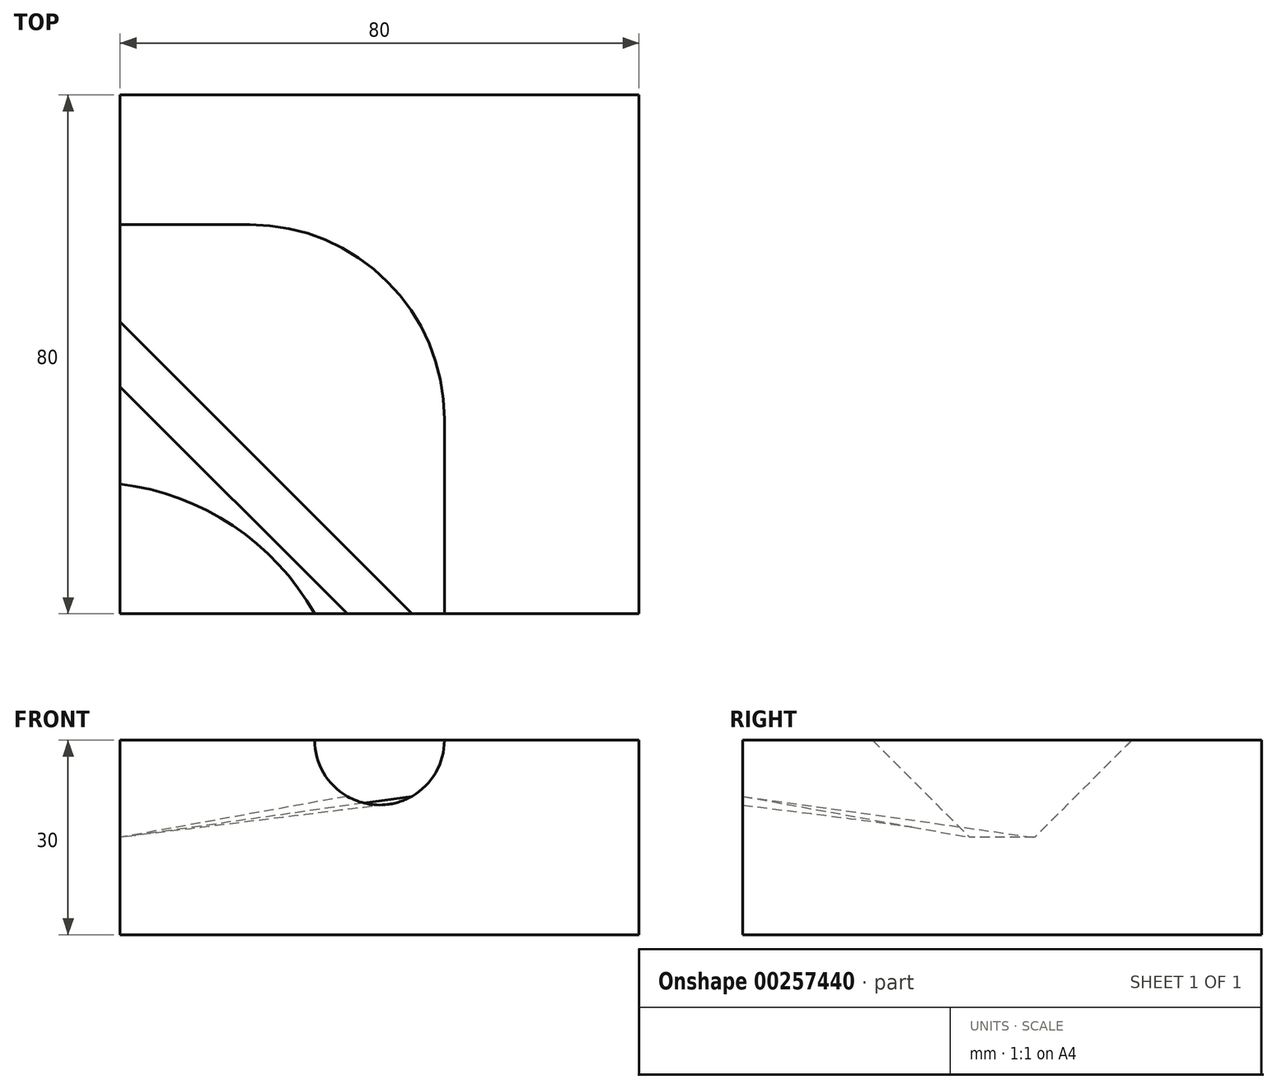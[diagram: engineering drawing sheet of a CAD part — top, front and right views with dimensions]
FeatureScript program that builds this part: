
annotation { "Feature Type Name" : "Feature", "Feature Type Description" : "" }
export const myFeature = defineFeature(function(context is Context, id is Id, definition is map)
    precondition{}
    {
        {
            var Q0;
            Q0=qCreatedBy(makeId("Top.planeOp"),FACE);
            var sketch = newSketch(context, id + "F0", { "sketchPlane" : qUnion([Q0])});
            skLineSegment(sketch, "E0.bottom", {"start": v(40, 40) * mm, "end": v(-40, 40) * mm});
            skLineSegment(sketch, "E0.top", {"start": v(40, -40) * mm, "end": v(-40, -40) * mm});
            skLineSegment(sketch, "E0.left", {"start": v(40, 40) * mm, "end": v(40, -40) * mm});
            skLineSegment(sketch, "E0.right", {"start": v(-40, 40) * mm, "end": v(-40, -40) * mm});
            skPoint(sketch, "E0.middle", {"position": v(0, 0) * mm});
            skSolve(sketch);
        }
        {
            var Q0;
            Q0=makeQuery(id+"F0.imprint","IMPRINT",FACE,{"disambiguationData":[TD([[makeQuery(id+"F0.imprint","IMPRINT",EDGE,{"derivedFrom":sQuery(id+"F0.wireOp",EDGE,"E0.bottom")}),1.0]])]});
            extrude(context, id + "F1", {"entities" : qUnion([Q0]), "depth" : 30 * mm});
        }
        {
            var Q0;
            Q0=makeQuery(id+"F1.opExtrude","SWEPT_FACE",FACE,{"disambiguationData":[OSD([sQuery(id+"F0.wireOp",EDGE,"E0.top")])]});
            var sketch = newSketch(context, id + "F2", { "sketchPlane" : qUnion([Q0])});
            skArc(sketch, "E1", {"start": v(-10, 30) * mm, "mid": v(0, 20) * mm, "end": v(10, 30) * mm});
            skLineSegment(sketch, "E2", {"start": v(-10, 30) * mm, "end": v(10, 30) * mm});
            skSolve(sketch);
        }
        {
            var Q0;
            Q0=makeQuery(id+"F1.opExtrude","SWEPT_FACE",FACE,{"disambiguationData":[OSD([sQuery(id+"F0.wireOp",EDGE,"E0.right")])]});
            var sketch = newSketch(context, id + "F3", { "sketchPlane" : qUnion([Q0])});
            skLineSegment(sketch, "E3", {"start": v(0, -9.8) * mm, "end": v(0, 51.9) * mm, "construction": true});
            skPoint(sketch, "E3.startSnap0", {"position": v(0, 0) * mm});
            skLineSegment(sketch, "E4", {"start": v(-5, 15) * mm, "end": v(5, 15) * mm});
            skLineSegment(sketch, "E5.0", {"start": v(20, -9.8) * mm, "end": v(20, 51.9) * mm, "construction": true});
            skLineSegment(sketch, "E6.MirrorCS", {"start": v(-20, -9.8) * mm, "end": v(-20, 51.9) * mm, "construction": true});
            skLineSegment(sketch, "E7", {"start": v(-20, 30) * mm, "end": v(-5, 15) * mm});
            skLineSegment(sketch, "E8.MirrorCS", {"start": v(20, 30) * mm, "end": v(5, 15) * mm});
            skSolve(sketch);
        }
        {
            var Q0;
            Q0=makeQuery(id+"F1.opExtrude","CAP_FACE",FACE,{"disambiguationData":[OSD([sQuery(id+"F0.wireOp",EDGE,"E0.bottom"),sQuery(id+"F0.wireOp",EDGE,"E0.top"),sQuery(id+"F0.wireOp",EDGE,"E0.left"),sQuery(id+"F0.wireOp",EDGE,"E0.right")])],"isStart":false});
            var sketch = newSketch(context, id + "F4", { "sketchPlane" : qUnion([Q0])});
            skLineSegment(sketch, "E9", {"start": v(-40, 20) * mm, "end": v(-20, 20) * mm});
            skLineSegment(sketch, "E10.0", {"start": v(-10, -40) * mm, "end": v(10, -40) * mm});
            skLineSegment(sketch, "E11.0", {"start": v(-40, -20) * mm, "end": v(-40, -5) * mm});
            skLineSegment(sketch, "E11.1", {"start": v(-40, 5) * mm, "end": v(-40, -5) * mm});
            skLineSegment(sketch, "E11.2", {"start": v(-40, 20) * mm, "end": v(-40, 5) * mm});
            skLineSegment(sketch, "E12", {"start": v(10, -40) * mm, "end": v(10, -10) * mm});
            skArc(sketch, "E13", {"start": v(10, -10) * mm, "mid": v(1.21, 11.21) * mm, "end": v(-20, 20) * mm});
            skArc(sketch, "E14", {"start": v(-10, -40) * mm, "mid": v(-22.62, -26.43) * mm, "end": v(-40, -20) * mm});
            skSolve(sketch);
        }
        {
            var Q0;
            {var subQ4=sQuery(id+"F4.wireOp",EDGE,"E9");Q0=makeQuery(id+"F4.imprint","IMPRINT",FACE,{"disambiguationData":[TD([[makeQuery(id+"F4.imprint","IMPRINT",EDGE,{"derivedFrom":subQ4}),1.0]])]});}
            var sketch = newSketch(context, id + "F5", { "sketchPlane" : qUnion([Q0])});
            skLineSegment(sketch, "E15.0", {"start": v(-40, 20) * mm, "end": v(-20, 20) * mm});
            skArc(sketch, "E15.1", {"start": v(10, -10) * mm, "mid": v(1.21, 11.21) * mm, "end": v(-20, 20) * mm});
            skLineSegment(sketch, "E15.2", {"start": v(10, -40) * mm, "end": v(10, -10) * mm});
            skSolve(sketch);
        }
        {
            var Q1;
            Q1=makeQuery(id+"F2.imprint","IMPRINT",FACE,{"disambiguationData":[TD([[makeQuery(id+"F2.imprint","IMPRINT",EDGE,{"derivedFrom":sQuery(id+"F2.wireOp",EDGE,"E1")}),1.0]])]});
            var Q2;
            Q2=makeQuery(id+"F3.imprint","IMPRINT",FACE,{"disambiguationData":[TD([[makeQuery(id+"F3.imprint","IMPRINT",EDGE,{"derivedFrom":sQuery(id+"F3.wireOp",EDGE,"E4")}),1.0]])]});
            var Q3;
            Q3=sQuery(id+"F4.wireOp",EDGE,"E14");
            var Q4;
            Q4 = qConstructionFilter(qBodyType(qCreatedBy(id + "F5" ,EDGE), BodyType.WIRE), ConstructionObject.NO);
            loft(context, id + "F6", {"operationType" : NewBodyOperationType.REMOVE, "addGuides" : true, "sheetProfilesArray" : [{ "sheetProfileEntities" : qUnion([Q1]) }, { "sheetProfileEntities" : qUnion([Q2]) }], "guidesArray" : [{ "guideEntities" : qUnion([Q3]), "guideDerivativeType" : LoftGuideDerivativeType.DEFAULT, "guideDerivativeMagnitude" : 1 }, { "guideEntities" : qUnion([Q4]), "guideDerivativeType" : LoftGuideDerivativeType.DEFAULT, "guideDerivativeMagnitude" : 1 }]});
        }
    });
